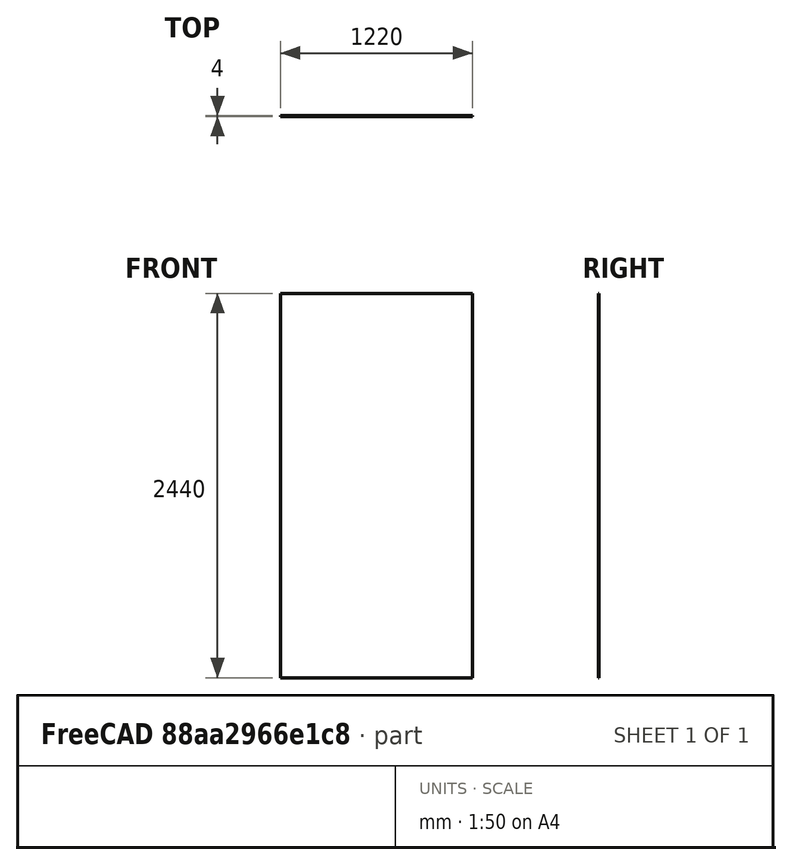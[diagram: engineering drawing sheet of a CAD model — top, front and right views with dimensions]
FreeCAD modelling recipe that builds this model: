
FCSTD DOCUMENT  (FreeCAD 0.21R33694 (Git))
Label: aristarchus_parametric_v2
License: All rights reserved
LicenseURL: http://en.wikipedia.org/wiki/All_rights_reserved
objects: Sketcher::SketchObject×2, PartDesign::Body×2, Spreadsheet::Sheet×1, PartDesign::Pad×1
note: 6 computed .brp shape members not serialized (recipe doc carries the construction recipe); baked Part::Feature solids carry a one-line shape summary decoded from their .brp

FEATURE [Sketcher::SketchObject] Sketch  label="plywood_sheet_sketch"
  FullyConstrained = true
  MapMode = 5
  Placement = pos=(0,0,0) rot=(1,0,0;1.5708rad)
  Support = -> [XZ_Plane]
  expr: Constraints[8] = <<d>>.sheet_width
  expr: Constraints[9] = <<d>>.sheet_height
  sketch-geometry (4):
    g0: LineSegment StartX=-610 StartY=1220 StartZ=0 EndX=610 EndY=1220 EndZ=0
    g1: LineSegment StartX=610 StartY=1220 StartZ=0 EndX=610 EndY=-1220 EndZ=0
    g2: LineSegment StartX=610 StartY=-1220 StartZ=0 EndX=-610 EndY=-1220 EndZ=0
    g3: LineSegment StartX=-610 StartY=-1220 StartZ=0 EndX=-610 EndY=1220 EndZ=0
  constraints (11):
    c: Coincident(g0,g1)
    c: Coincident(g1,g2)
    c: Coincident(g2,g3)
    c: Coincident(g3,g0)
    c: Horizontal(g0)
    c: Horizontal(g2)
    c: Vertical(g1)
    c: Vertical(g3)
    c: DistanceX(g2,g2) = 1220
    c: DistanceY(g1,g1) = 2440
    c: Symmetric(g0,g2,g-1)
FEATURE [Spreadsheet::Sheet] Spreadsheet  label="d"
  cells = A1='sheet_width; B1(sheet_width)=1220; C1='mm; A2='sheet_height; B2(sheet_height)=2440; C2='mm; A3='sheet_thickness; B3(sheet_thickness)=4; C3='mm; A4='batten_width; B4(batten_width)=63; C4='mm; A5='batten_height; B5(batten_height)=1200; C5='mm; A6='batten_thickness; B6(batten_thickness)=38; C6='mm
FEATURE [PartDesign::Pad] Pad
  Direction = (0,-1,2e-16)
  Length = 4
  Length2 = 10
  Placement = pos=(0,0,0) rot=(1,0,0;1.5708rad)
  Profile = -> Sketch
  ReferenceAxis = -> Sketch [N_Axis]
  Type = 0
  expr: Length = <<d>>.sheet_thickness
FEATURE [Sketcher::SketchObject] Sketch001
  FullyConstrained = true
  MapMode = 5
  Placement = pos=(0,-4,9e-16) rot=(1,0,0;1.5708rad)
  Support = -> [Pad]
  expr: Constraints[10] = <<d>>.sheet_height / 2
  expr: Constraints[11] = <<d>>.batten_height / 2
  expr: Constraints[8] = <<d>>.batten_width
  expr: Constraints[9] = <<d>>.batten_height
  sketch-geometry (4):
    g0: LineSegment StartX=-600 StartY=-1157 StartZ=0 EndX=600 EndY=-1157 EndZ=0
    g1: LineSegment StartX=600 StartY=-1157 StartZ=0 EndX=600 EndY=-1220 EndZ=0
    g2: LineSegment StartX=600 StartY=-1220 StartZ=0 EndX=-600 EndY=-1220 EndZ=0
    g3: LineSegment StartX=-600 StartY=-1220 StartZ=0 EndX=-600 EndY=-1157 EndZ=0
  constraints (12):
    c: Coincident(g0,g1)
    c: Coincident(g1,g2)
    c: Coincident(g2,g3)
    c: Coincident(g3,g0)
    c: Horizontal(g0)
    c: Horizontal(g2)
    c: Vertical(g1)
    c: Vertical(g3)
    c: DistanceY(g1,g0) = 63
    c: DistanceX(g0,g0) = 1200
    c: DistanceY(g1,g-1) = 1220
    c: DistanceX(g-1,g0) = 600
FEATURE [PartDesign::Body] Body  label="plywood_sheet"
  Group = -> [Sketch,Pad,Sketch001]
  Origin = -> Origin
  Tip = -> Pad
FEATURE [PartDesign::Body] Body001  label="lower_batten"
  Origin = -> Origin001
